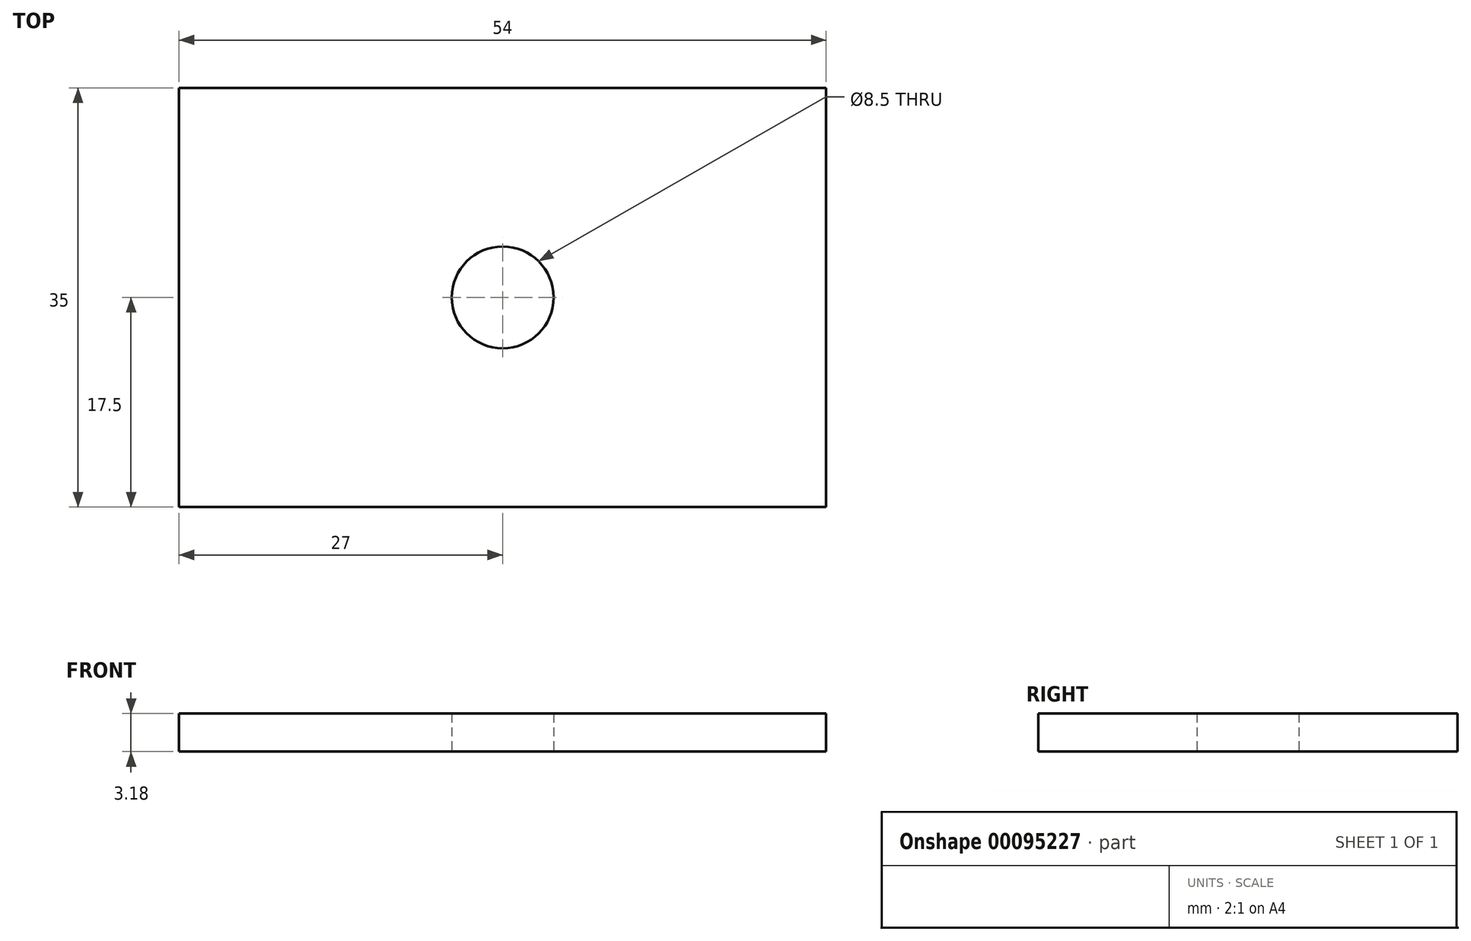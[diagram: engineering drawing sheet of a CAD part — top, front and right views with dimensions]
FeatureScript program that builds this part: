
annotation { "Feature Type Name" : "Feature", "Feature Type Description" : "" }
export const myFeature = defineFeature(function(context is Context, id is Id, definition is map)
    precondition{}
    {
        {
            var Q0;
            Q0=qCreatedBy(makeId("Top.planeOp"),FACE);
            var sketch = newSketch(context, id + "F0", { "sketchPlane" : qUnion([Q0])});
            skLineSegment(sketch, "E0.bottom", {"start": v(27, 17.5) * mm, "end": v(-27, 17.5) * mm});
            skLineSegment(sketch, "E0.top", {"start": v(27, -17.5) * mm, "end": v(-27, -17.5) * mm});
            skLineSegment(sketch, "E0.left", {"start": v(27, 17.5) * mm, "end": v(27, -17.5) * mm});
            skLineSegment(sketch, "E0.right", {"start": v(-27, 17.5) * mm, "end": v(-27, -17.5) * mm});
            skPoint(sketch, "E0.middle", {"position": v(0, 0) * mm});
            skCircle(sketch, "E1", {"center": v(0, 0) * mm, "radius": 4.25 * mm});
            skSolve(sketch);
        }
        {
            var Q0;
            Q0=makeQuery(id+"F0.imprint","IMPRINT",FACE,{"disambiguationData":[TD([[makeQuery(id+"F0.imprint","IMPRINT",EDGE,{"derivedFrom":sQuery(id+"F0.wireOp",EDGE,"E0.bottom")}),1.0]])]});
            extrude(context, id + "F1", {"entities" : qUnion([Q0]), "depth" : 3.17 * mm});
        }
    });
